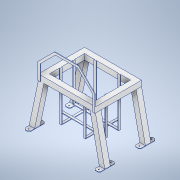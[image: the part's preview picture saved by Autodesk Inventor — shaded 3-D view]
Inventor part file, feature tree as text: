
AUTODESK INVENTOR PART (.ipt)
format: ipt  version: 2020 (Build 240168000, 168)  size: 413,184 bytes
history: native  units: mm
features: extrude x10, sketch x10, shell x1, chamfer x1
ambient origin geometry x8: Origin, YZ Plane, XZ Plane, XY Plane, X Axis, Y Axis, Z Axis, Center Point
bodies: Volumenkörper1 (feature_tree)
feature tree (22):
  extrude  "Extrusion1"  Depth=320.0mm
  extrude  "Extrusion2"  Depth=50.0mm
  extrude  "Extrusion3"  Depth=420.0mm
  shell  "Wandung2"  Thickness=50.0mm
  extrude  "Extrusion4"  Depth=85.0mm
  chamfer  "Fase1"  Distance=50.0mm
  extrude  "Extrusion5"  Depth=420.0mm TaperAngle=0.0deg
  extrude  "Extrusion6"  Depth=50.0mm
  extrude  "Extrusion7"  Depth=320.0mm
  extrude  "Extrusion8"  Depth=5.0mm TaperAngle=0.0deg
  extrude  "Extrusion9"  Depth=5.0mm
  extrude  "Extrusion10"  Depth=50.0mm
  sketch  "Skizze1"  dims[d0=420.0mm d1=320.0mm]
  sketch  "Skizze2"  dims[d2=50.0mm d3=50.0mm]
  sketch  "Skizze3"  dims[d4=520.0mm d5=420.0mm d6=50.0mm d7=0.0mm]
  sketch  "Skizze4"  dims[d8=400.0mm d9=85.0mm]
  sketch  "Skizze5"  dims[d10=90.0deg]
  sketch  "Skizze6"  dims[d11=50.0mm]
  sketch  "Skizze7"  dims[d12=400.0mm]
  sketch  "Skizze8"  dims[d13=90.0deg]
  sketch  "Skizze9"  dims[d14=85.0mm]
  sketch  "Skizze10"  dims[d15=90.0deg d16=50.0mm d17=420.0mm d18=0.0mm d19=50.0mm d20=320.0mm d21=2000.0mm d22=0.0mm d24=5.0mm d25=50.0mm d26=50.0mm d27=150.0mm d28=5.0mm d29=0.0mm d30=12.5mm d31=2.0mm d32=45.0deg d33=20.0mm d34=9.0mm d35=5.0mm d36=0.0mm d37=90.0mm d38=90.0mm d39=20.0mm d40=5.0mm d41=5.0mm d42=20.0mm d43=345.0mm d44=0.0mm d45=5.0mm d46=5.0mm d47=5.0mm d48=345.0mm d49=0.0mm d50=5.0mm d51=0.0mm d52=5.0mm d53=0.0mm d54=20.0mm d55=150.0mm d56=20.0mm d57=150.0mm d58=45.0deg d59=135.0deg d60=250.0mm d61=90.0deg d62=20.0mm d63=20.0mm d64=20.0mm d65=20.0mm d66=20.0mm d67=5.0mm d68=0.0mm]
